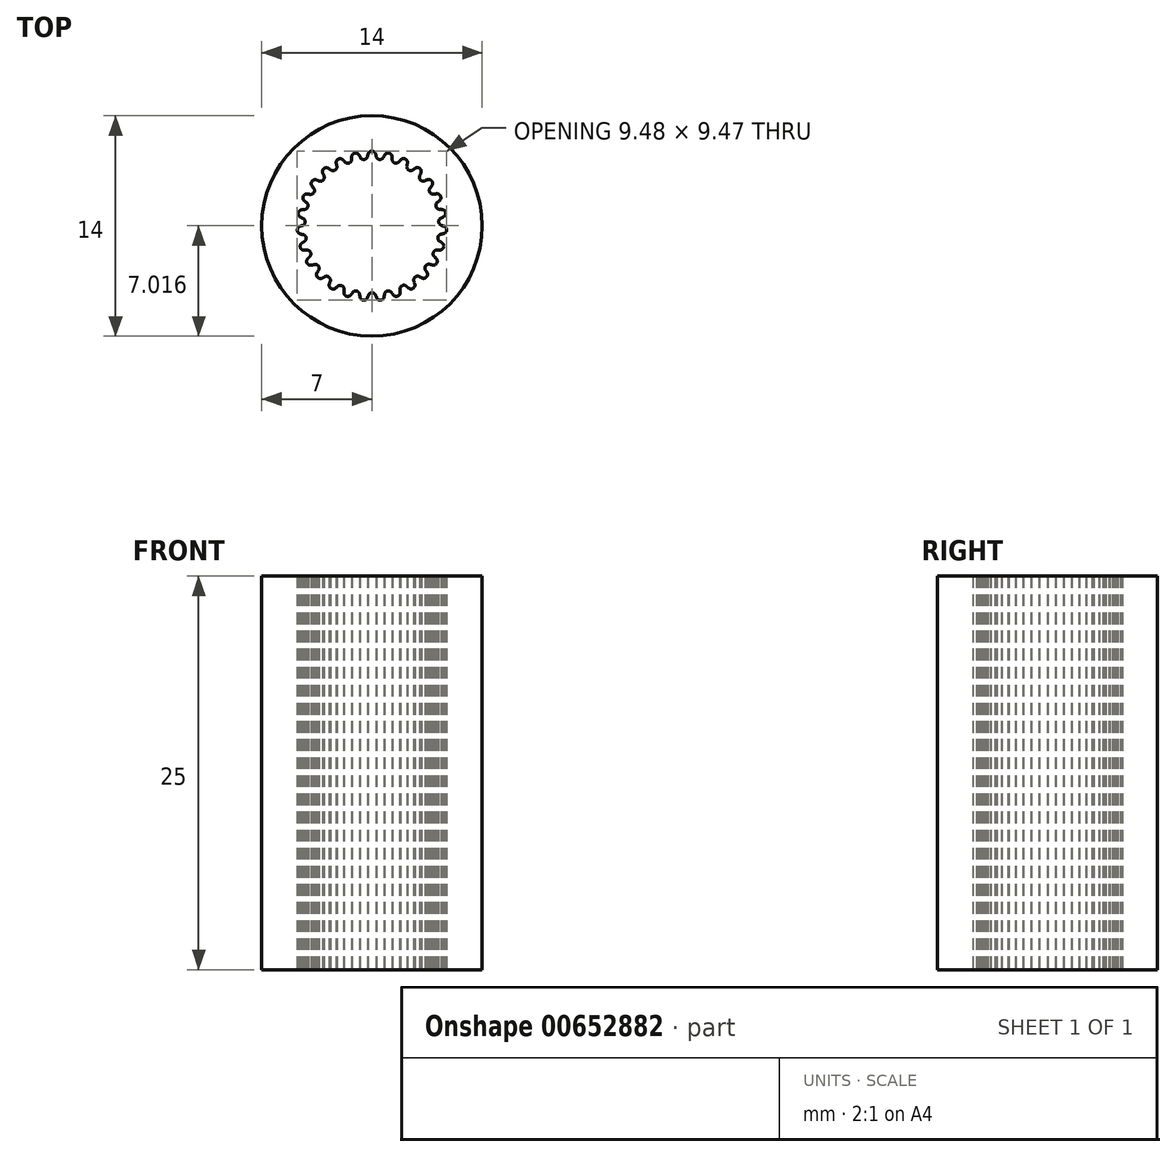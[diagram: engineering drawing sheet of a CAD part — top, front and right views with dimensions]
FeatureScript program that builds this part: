
annotation { "Feature Type Name" : "Feature", "Feature Type Description" : "" }
export const myFeature = defineFeature(function(context is Context, id is Id, definition is map)
    precondition{}
    {
        {
            var Q0;
            Q0=qCreatedBy(makeId("Top.planeOp"),FACE);
            var sketch = newSketch(context, id + "F0", { "sketchPlane" : qUnion([Q0])});
            skCircle(sketch, "E0", {"center": v(0, 0) * mm, "radius": 4.5 * mm});
            skCircle(sketch, "E1", {"center": v(0, 0) * mm, "radius": 7 * mm});
            skCircle(sketch, "E2", {"center": v(0, 4.5) * mm, "radius": 0.25 * mm});
            skCircle(sketch, "E3.1.0", {"center": v(-0.52, 4.47) * mm, "radius": 0.25 * mm});
            skCircle(sketch, "E3.2.0", {"center": v(-1.04, 4.38) * mm, "radius": 0.25 * mm});
            skCircle(sketch, "E3.3.0", {"center": v(-1.54, 4.23) * mm, "radius": 0.25 * mm});
            skCircle(sketch, "E3.4.0", {"center": v(-2.02, 4.02) * mm, "radius": 0.25 * mm});
            skCircle(sketch, "E3.5.0", {"center": v(-2.47, 3.76) * mm, "radius": 0.25 * mm});
            skCircle(sketch, "E3.6.0", {"center": v(-2.9, 3.45) * mm, "radius": 0.25 * mm});
            skCircle(sketch, "E3.7.0", {"center": v(-3.27, 3.09) * mm, "radius": 0.25 * mm});
            skCircle(sketch, "E3.8.0", {"center": v(-3.61, 2.69) * mm, "radius": 0.25 * mm});
            skCircle(sketch, "E3.9.0", {"center": v(-3.9, 2.25) * mm, "radius": 0.25 * mm});
            skCircle(sketch, "E3.10.0", {"center": v(-4.13, 1.78) * mm, "radius": 0.25 * mm});
            skCircle(sketch, "E3.11.0", {"center": v(-4.31, 1.29) * mm, "radius": 0.25 * mm});
            skCircle(sketch, "E3.12.0", {"center": v(-4.43, 0.78) * mm, "radius": 0.25 * mm});
            skCircle(sketch, "E3.13.0", {"center": v(-4.5, 0.26) * mm, "radius": 0.25 * mm});
            skCircle(sketch, "E3.14.0", {"center": v(-4.5, -0.27) * mm, "radius": 0.25 * mm});
            skCircle(sketch, "E3.15.0", {"center": v(-4.43, -0.79) * mm, "radius": 0.25 * mm});
            skCircle(sketch, "E3.16.0", {"center": v(-4.3, -1.3) * mm, "radius": 0.25 * mm});
            skCircle(sketch, "E3.17.0", {"center": v(-4.13, -1.79) * mm, "radius": 0.25 * mm});
            skCircle(sketch, "E3.18.0", {"center": v(-3.9, -2.25) * mm, "radius": 0.25 * mm});
            skCircle(sketch, "E3.19.0", {"center": v(-3.6, -2.7) * mm, "radius": 0.25 * mm});
            skLineSegment(sketch, "E3.anchor1", {"start": v(0, 0) * mm, "end": v(0, 4.5) * mm, "construction": true});
            skLineSegment(sketch, "E3.anchor2", {"start": v(0, 0) * mm, "end": v(0.5, 4.47) * mm, "construction": true});
            skCircle(sketch, "E4.1.20.0", {"center": v(-3.27, -3.1) * mm, "radius": 0.25 * mm});
            skCircle(sketch, "E4.1.21.0", {"center": v(-2.89, -3.45) * mm, "radius": 0.25 * mm});
            skCircle(sketch, "E4.1.22.0", {"center": v(-2.47, -3.76) * mm, "radius": 0.25 * mm});
            skCircle(sketch, "E4.1.23.0", {"center": v(-2.01, -4.02) * mm, "radius": 0.25 * mm});
            skCircle(sketch, "E4.1.24.0", {"center": v(-1.53, -4.23) * mm, "radius": 0.25 * mm});
            skCircle(sketch, "E4.1.25.0", {"center": v(-1.03, -4.38) * mm, "radius": 0.25 * mm});
            skCircle(sketch, "E4.1.26.0", {"center": v(-0.52, -4.47) * mm, "radius": 0.25 * mm});
            skCircle(sketch, "E4.1.27.0", {"center": v(0, -4.5) * mm, "radius": 0.25 * mm});
            skCircle(sketch, "E4.1.28.0", {"center": v(0.53, -4.47) * mm, "radius": 0.25 * mm});
            skCircle(sketch, "E4.1.29.0", {"center": v(1.04, -4.38) * mm, "radius": 0.25 * mm});
            skCircle(sketch, "E4.1.30.0", {"center": v(1.55, -4.23) * mm, "radius": 0.25 * mm});
            skCircle(sketch, "E4.1.31.0", {"center": v(2.03, -4.02) * mm, "radius": 0.25 * mm});
            skCircle(sketch, "E4.1.32.0", {"center": v(2.48, -3.76) * mm, "radius": 0.25 * mm});
            skCircle(sketch, "E4.1.33.0", {"center": v(2.9, -3.44) * mm, "radius": 0.25 * mm});
            skCircle(sketch, "E4.1.34.0", {"center": v(3.28, -3.08) * mm, "radius": 0.25 * mm});
            skCircle(sketch, "E4.1.35.0", {"center": v(3.61, -2.68) * mm, "radius": 0.25 * mm});
            skCircle(sketch, "E4.1.36.0", {"center": v(3.9, -2.24) * mm, "radius": 0.25 * mm});
            skCircle(sketch, "E4.1.37.0", {"center": v(4.14, -1.77) * mm, "radius": 0.25 * mm});
            skCircle(sketch, "E4.1.38.0", {"center": v(4.31, -1.28) * mm, "radius": 0.25 * mm});
            skCircle(sketch, "E4.1.39.0", {"center": v(4.43, -0.77) * mm, "radius": 0.25 * mm});
            skCircle(sketch, "E5.1.40.0", {"center": v(4.5, -0.25) * mm, "radius": 0.25 * mm});
            skCircle(sketch, "E5.1.41.0", {"center": v(4.5, 0.27) * mm, "radius": 0.25 * mm});
            skCircle(sketch, "E5.1.42.0", {"center": v(4.43, 0.8) * mm, "radius": 0.25 * mm});
            skCircle(sketch, "E6.1.43.0", {"center": v(4.3, 1.3) * mm, "radius": 0.25 * mm});
            skCircle(sketch, "E6.1.44.0", {"center": v(4.13, 1.8) * mm, "radius": 0.25 * mm});
            skCircle(sketch, "E7.1.45.0", {"center": v(3.9, 2.26) * mm, "radius": 0.25 * mm});
            skCircle(sketch, "E7.1.46.0", {"center": v(3.6, 2.7) * mm, "radius": 0.25 * mm});
            skCircle(sketch, "E7.1.47.0", {"center": v(3.27, 3.1) * mm, "radius": 0.25 * mm});
            skCircle(sketch, "E7.1.48.0", {"center": v(2.88, 3.45) * mm, "radius": 0.25 * mm});
            skCircle(sketch, "E7.1.49.0", {"center": v(2.46, 3.77) * mm, "radius": 0.25 * mm});
            skCircle(sketch, "E8.1.50.0", {"center": v(2, 4.03) * mm, "radius": 0.25 * mm});
            skCircle(sketch, "E8.1.51.0", {"center": v(1.53, 4.23) * mm, "radius": 0.25 * mm});
            skCircle(sketch, "E8.1.52.0", {"center": v(1.03, 4.38) * mm, "radius": 0.25 * mm});
            skCircle(sketch, "E8.1.53.0", {"center": v(0.5, 4.47) * mm, "radius": 0.25 * mm});
            skSolve(sketch);
        }
        {
            var Q0;
            Q0 = qSketchRegion(id + "F0", true);
            var Q1;
            {var subQ0=sQuery(id+"F0.wireOp",EDGE,"E4.1.33.0");var subQ1=sQuery(id+"F0.wireOp",EDGE,"E0");var subQ2=makeQuery(id+"F0.imprint","INTERSECT",VERTEX,{"disambiguationData":[OD(0.0)],"derivedFrom":[subQ1,subQ0]});Q1=makeQuery(id+"F0.imprint","IMPRINT",FACE,{"disambiguationData":[TD([[makeQuery(id+"F0.imprint","IMPRINT",EDGE,{"disambiguationData":[TD([[subQ2,-1.0]])],"derivedFrom":subQ1}),1.0]])]});}
            var Q2;
            {var subQ0=sQuery(id+"F0.wireOp",EDGE,"E4.1.33.0");var subQ1=sQuery(id+"F0.wireOp",EDGE,"E0");var subQ2=makeQuery(id+"F0.imprint","INTERSECT",VERTEX,{"disambiguationData":[OD(0.0)],"derivedFrom":[subQ1,subQ0]});Q2=makeQuery(id+"F0.imprint","IMPRINT",FACE,{"disambiguationData":[TD([[makeQuery(id+"F0.imprint","IMPRINT",EDGE,{"disambiguationData":[TD([[subQ2,-1.0]])],"derivedFrom":subQ1}),-1.0]])]});}
            var Q3;
            {var subQ0=sQuery(id+"F0.wireOp",EDGE,"E4.1.31.0");var subQ1=sQuery(id+"F0.wireOp",EDGE,"E0");var subQ2=makeQuery(id+"F0.imprint","INTERSECT",VERTEX,{"disambiguationData":[OD(0.0)],"derivedFrom":[subQ1,subQ0]});Q3=makeQuery(id+"F0.imprint","IMPRINT",FACE,{"disambiguationData":[TD([[makeQuery(id+"F0.imprint","IMPRINT",EDGE,{"disambiguationData":[TD([[subQ2,-1.0]])],"derivedFrom":subQ1}),1.0]])]});}
            var Q4;
            {var subQ0=sQuery(id+"F0.wireOp",EDGE,"E4.1.31.0");var subQ1=sQuery(id+"F0.wireOp",EDGE,"E0");var subQ2=makeQuery(id+"F0.imprint","INTERSECT",VERTEX,{"disambiguationData":[OD(0.0)],"derivedFrom":[subQ1,subQ0]});Q4=makeQuery(id+"F0.imprint","IMPRINT",FACE,{"disambiguationData":[TD([[makeQuery(id+"F0.imprint","IMPRINT",EDGE,{"disambiguationData":[TD([[subQ2,-1.0]])],"derivedFrom":subQ1}),-1.0]])]});}
            var Q5;
            {var subQ0=sQuery(id+"F0.wireOp",EDGE,"E4.1.29.0");var subQ1=sQuery(id+"F0.wireOp",EDGE,"E0");var subQ2=makeQuery(id+"F0.imprint","INTERSECT",VERTEX,{"disambiguationData":[OD(0.0)],"derivedFrom":[subQ1,subQ0]});Q5=makeQuery(id+"F0.imprint","IMPRINT",FACE,{"disambiguationData":[TD([[makeQuery(id+"F0.imprint","IMPRINT",EDGE,{"disambiguationData":[TD([[subQ2,-1.0]])],"derivedFrom":subQ1}),-1.0]])]});}
            var Q6;
            {var subQ0=sQuery(id+"F0.wireOp",EDGE,"E4.1.29.0");var subQ1=sQuery(id+"F0.wireOp",EDGE,"E0");var subQ2=makeQuery(id+"F0.imprint","INTERSECT",VERTEX,{"disambiguationData":[OD(0.0)],"derivedFrom":[subQ1,subQ0]});Q6=makeQuery(id+"F0.imprint","IMPRINT",FACE,{"disambiguationData":[TD([[makeQuery(id+"F0.imprint","IMPRINT",EDGE,{"disambiguationData":[TD([[subQ2,-1.0]])],"derivedFrom":subQ1}),1.0]])]});}
            var Q7;
            {var subQ0=sQuery(id+"F0.wireOp",EDGE,"E4.1.27.0");var subQ1=sQuery(id+"F0.wireOp",EDGE,"E0");var subQ2=makeQuery(id+"F0.imprint","INTERSECT",VERTEX,{"disambiguationData":[OD(0.0)],"derivedFrom":[subQ1,subQ0]});Q7=makeQuery(id+"F0.imprint","IMPRINT",FACE,{"disambiguationData":[TD([[makeQuery(id+"F0.imprint","IMPRINT",EDGE,{"disambiguationData":[TD([[subQ2,-1.0]])],"derivedFrom":subQ1}),1.0]])]});}
            var Q8;
            {var subQ0=sQuery(id+"F0.wireOp",EDGE,"E4.1.27.0");var subQ1=sQuery(id+"F0.wireOp",EDGE,"E0");var subQ2=makeQuery(id+"F0.imprint","INTERSECT",VERTEX,{"disambiguationData":[OD(0.0)],"derivedFrom":[subQ1,subQ0]});Q8=makeQuery(id+"F0.imprint","IMPRINT",FACE,{"disambiguationData":[TD([[makeQuery(id+"F0.imprint","IMPRINT",EDGE,{"disambiguationData":[TD([[subQ2,-1.0]])],"derivedFrom":subQ1}),-1.0]])]});}
            var Q9;
            {var subQ0=sQuery(id+"F0.wireOp",EDGE,"E4.1.25.0");var subQ1=sQuery(id+"F0.wireOp",EDGE,"E0");var subQ2=makeQuery(id+"F0.imprint","INTERSECT",VERTEX,{"disambiguationData":[OD(0.0)],"derivedFrom":[subQ1,subQ0]});Q9=makeQuery(id+"F0.imprint","IMPRINT",FACE,{"disambiguationData":[TD([[makeQuery(id+"F0.imprint","IMPRINT",EDGE,{"disambiguationData":[TD([[subQ2,-1.0]])],"derivedFrom":subQ1}),1.0]])]});}
            var Q10;
            {var subQ0=sQuery(id+"F0.wireOp",EDGE,"E4.1.25.0");var subQ1=sQuery(id+"F0.wireOp",EDGE,"E0");var subQ2=makeQuery(id+"F0.imprint","INTERSECT",VERTEX,{"disambiguationData":[OD(0.0)],"derivedFrom":[subQ1,subQ0]});Q10=makeQuery(id+"F0.imprint","IMPRINT",FACE,{"disambiguationData":[TD([[makeQuery(id+"F0.imprint","IMPRINT",EDGE,{"disambiguationData":[TD([[subQ2,-1.0]])],"derivedFrom":subQ1}),-1.0]])]});}
            var Q11;
            {var subQ0=sQuery(id+"F0.wireOp",EDGE,"E4.1.35.0");var subQ1=sQuery(id+"F0.wireOp",EDGE,"E0");var subQ2=makeQuery(id+"F0.imprint","INTERSECT",VERTEX,{"disambiguationData":[OD(0.0)],"derivedFrom":[subQ1,subQ0]});Q11=makeQuery(id+"F0.imprint","IMPRINT",FACE,{"disambiguationData":[TD([[makeQuery(id+"F0.imprint","IMPRINT",EDGE,{"disambiguationData":[TD([[subQ2,-1.0]])],"derivedFrom":subQ1}),1.0]])]});}
            var Q12;
            {var subQ0=sQuery(id+"F0.wireOp",EDGE,"E4.1.35.0");var subQ1=sQuery(id+"F0.wireOp",EDGE,"E0");var subQ2=makeQuery(id+"F0.imprint","INTERSECT",VERTEX,{"disambiguationData":[OD(0.0)],"derivedFrom":[subQ1,subQ0]});Q12=makeQuery(id+"F0.imprint","IMPRINT",FACE,{"disambiguationData":[TD([[makeQuery(id+"F0.imprint","IMPRINT",EDGE,{"disambiguationData":[TD([[subQ2,-1.0]])],"derivedFrom":subQ1}),-1.0]])]});}
            var Q13;
            {var subQ0=sQuery(id+"F0.wireOp",EDGE,"E4.1.37.0");var subQ1=sQuery(id+"F0.wireOp",EDGE,"E0");var subQ2=makeQuery(id+"F0.imprint","INTERSECT",VERTEX,{"disambiguationData":[OD(0.0)],"derivedFrom":[subQ1,subQ0]});Q13=makeQuery(id+"F0.imprint","IMPRINT",FACE,{"disambiguationData":[TD([[makeQuery(id+"F0.imprint","IMPRINT",EDGE,{"disambiguationData":[TD([[subQ2,-1.0]])],"derivedFrom":subQ1}),1.0]])]});}
            var Q14;
            {var subQ0=sQuery(id+"F0.wireOp",EDGE,"E4.1.37.0");var subQ1=sQuery(id+"F0.wireOp",EDGE,"E0");var subQ2=makeQuery(id+"F0.imprint","INTERSECT",VERTEX,{"disambiguationData":[OD(0.0)],"derivedFrom":[subQ1,subQ0]});Q14=makeQuery(id+"F0.imprint","IMPRINT",FACE,{"disambiguationData":[TD([[makeQuery(id+"F0.imprint","IMPRINT",EDGE,{"disambiguationData":[TD([[subQ2,-1.0]])],"derivedFrom":subQ1}),-1.0]])]});}
            var Q15;
            {var subQ0=sQuery(id+"F0.wireOp",EDGE,"E4.1.39.0");var subQ1=sQuery(id+"F0.wireOp",EDGE,"E0");var subQ2=makeQuery(id+"F0.imprint","INTERSECT",VERTEX,{"disambiguationData":[OD(0.0)],"derivedFrom":[subQ1,subQ0]});Q15=makeQuery(id+"F0.imprint","IMPRINT",FACE,{"disambiguationData":[TD([[makeQuery(id+"F0.imprint","IMPRINT",EDGE,{"disambiguationData":[TD([[subQ2,-1.0]])],"derivedFrom":subQ1}),-1.0]])]});}
            var Q16;
            {var subQ0=sQuery(id+"F0.wireOp",EDGE,"E5.1.41.0");var subQ1=sQuery(id+"F0.wireOp",EDGE,"E0");var subQ2=makeQuery(id+"F0.imprint","INTERSECT",VERTEX,{"disambiguationData":[OD(0.0)],"derivedFrom":[subQ1,subQ0]});Q16=makeQuery(id+"F0.imprint","IMPRINT",FACE,{"disambiguationData":[TD([[makeQuery(id+"F0.imprint","IMPRINT",EDGE,{"disambiguationData":[TD([[subQ2,-1.0]])],"derivedFrom":subQ1}),-1.0]])]});}
            var Q17;
            {var subQ0=sQuery(id+"F0.wireOp",EDGE,"E4.1.39.0");var subQ1=sQuery(id+"F0.wireOp",EDGE,"E0");var subQ2=makeQuery(id+"F0.imprint","INTERSECT",VERTEX,{"disambiguationData":[OD(0.0)],"derivedFrom":[subQ1,subQ0]});Q17=makeQuery(id+"F0.imprint","IMPRINT",FACE,{"disambiguationData":[TD([[makeQuery(id+"F0.imprint","IMPRINT",EDGE,{"disambiguationData":[TD([[subQ2,-1.0]])],"derivedFrom":subQ1}),1.0]])]});}
            var Q18;
            {var subQ0=sQuery(id+"F0.wireOp",EDGE,"E6.1.43.0");var subQ1=sQuery(id+"F0.wireOp",EDGE,"E0");var subQ2=makeQuery(id+"F0.imprint","INTERSECT",VERTEX,{"disambiguationData":[OD(0.0)],"derivedFrom":[subQ1,subQ0]});Q18=makeQuery(id+"F0.imprint","IMPRINT",FACE,{"disambiguationData":[TD([[makeQuery(id+"F0.imprint","IMPRINT",EDGE,{"disambiguationData":[TD([[subQ2,-1.0]])],"derivedFrom":subQ1}),-1.0]])]});}
            var Q19;
            {var subQ0=sQuery(id+"F0.wireOp",EDGE,"E6.1.43.0");var subQ1=sQuery(id+"F0.wireOp",EDGE,"E0");var subQ2=makeQuery(id+"F0.imprint","INTERSECT",VERTEX,{"disambiguationData":[OD(0.0)],"derivedFrom":[subQ1,subQ0]});Q19=makeQuery(id+"F0.imprint","IMPRINT",FACE,{"disambiguationData":[TD([[makeQuery(id+"F0.imprint","IMPRINT",EDGE,{"disambiguationData":[TD([[subQ2,-1.0]])],"derivedFrom":subQ1}),1.0]])]});}
            var Q20;
            {var subQ0=sQuery(id+"F0.wireOp",EDGE,"E7.1.47.0");var subQ1=sQuery(id+"F0.wireOp",EDGE,"E0");var subQ2=makeQuery(id+"F0.imprint","INTERSECT",VERTEX,{"disambiguationData":[OD(0.0)],"derivedFrom":[subQ1,subQ0]});Q20=makeQuery(id+"F0.imprint","IMPRINT",FACE,{"disambiguationData":[TD([[makeQuery(id+"F0.imprint","IMPRINT",EDGE,{"disambiguationData":[TD([[subQ2,-1.0]])],"derivedFrom":subQ1}),-1.0]])]});}
            var Q21;
            {var subQ0=sQuery(id+"F0.wireOp",EDGE,"E7.1.49.0");var subQ1=sQuery(id+"F0.wireOp",EDGE,"E0");var subQ2=makeQuery(id+"F0.imprint","INTERSECT",VERTEX,{"disambiguationData":[OD(0.0)],"derivedFrom":[subQ1,subQ0]});Q21=makeQuery(id+"F0.imprint","IMPRINT",FACE,{"disambiguationData":[TD([[makeQuery(id+"F0.imprint","IMPRINT",EDGE,{"disambiguationData":[TD([[subQ2,-1.0]])],"derivedFrom":subQ1}),-1.0]])]});}
            var Q22;
            {var subQ0=sQuery(id+"F0.wireOp",EDGE,"E7.1.49.0");var subQ1=sQuery(id+"F0.wireOp",EDGE,"E0");var subQ2=makeQuery(id+"F0.imprint","INTERSECT",VERTEX,{"disambiguationData":[OD(0.0)],"derivedFrom":[subQ1,subQ0]});Q22=makeQuery(id+"F0.imprint","IMPRINT",FACE,{"disambiguationData":[TD([[makeQuery(id+"F0.imprint","IMPRINT",EDGE,{"disambiguationData":[TD([[subQ2,-1.0]])],"derivedFrom":subQ1}),1.0]])]});}
            var Q23;
            {var subQ0=sQuery(id+"F0.wireOp",EDGE,"E3.1.0");var subQ1=sQuery(id+"F0.wireOp",EDGE,"E0");var subQ2=makeQuery(id+"F0.imprint","INTERSECT",VERTEX,{"disambiguationData":[OD(0.0)],"derivedFrom":[subQ1,subQ0]});Q23=makeQuery(id+"F0.imprint","IMPRINT",FACE,{"disambiguationData":[TD([[makeQuery(id+"F0.imprint","IMPRINT",EDGE,{"disambiguationData":[TD([[subQ2,-1.0]])],"derivedFrom":subQ1}),1.0]])]});}
            var Q24;
            {var subQ0=sQuery(id+"F0.wireOp",EDGE,"E3.1.0");var subQ1=sQuery(id+"F0.wireOp",EDGE,"E0");var subQ2=makeQuery(id+"F0.imprint","INTERSECT",VERTEX,{"disambiguationData":[OD(0.0)],"derivedFrom":[subQ1,subQ0]});Q24=makeQuery(id+"F0.imprint","IMPRINT",FACE,{"disambiguationData":[TD([[makeQuery(id+"F0.imprint","IMPRINT",EDGE,{"disambiguationData":[TD([[subQ2,-1.0]])],"derivedFrom":subQ1}),-1.0]])]});}
            var Q25;
            {var subQ0=sQuery(id+"F0.wireOp",EDGE,"E3.3.0");var subQ1=sQuery(id+"F0.wireOp",EDGE,"E0");var subQ2=makeQuery(id+"F0.imprint","INTERSECT",VERTEX,{"disambiguationData":[OD(0.0)],"derivedFrom":[subQ1,subQ0]});Q25=makeQuery(id+"F0.imprint","IMPRINT",FACE,{"disambiguationData":[TD([[makeQuery(id+"F0.imprint","IMPRINT",EDGE,{"disambiguationData":[TD([[subQ2,-1.0]])],"derivedFrom":subQ1}),-1.0]])]});}
            var Q26;
            {var subQ0=sQuery(id+"F0.wireOp",EDGE,"E3.3.0");var subQ1=sQuery(id+"F0.wireOp",EDGE,"E0");var subQ2=makeQuery(id+"F0.imprint","INTERSECT",VERTEX,{"disambiguationData":[OD(0.0)],"derivedFrom":[subQ1,subQ0]});Q26=makeQuery(id+"F0.imprint","IMPRINT",FACE,{"disambiguationData":[TD([[makeQuery(id+"F0.imprint","IMPRINT",EDGE,{"disambiguationData":[TD([[subQ2,-1.0]])],"derivedFrom":subQ1}),1.0]])]});}
            var Q27;
            {var subQ0=sQuery(id+"F0.wireOp",EDGE,"E4.1.23.0");var subQ1=sQuery(id+"F0.wireOp",EDGE,"E0");var subQ2=makeQuery(id+"F0.imprint","INTERSECT",VERTEX,{"disambiguationData":[OD(0.0)],"derivedFrom":[subQ1,subQ0]});Q27=makeQuery(id+"F0.imprint","IMPRINT",FACE,{"disambiguationData":[TD([[makeQuery(id+"F0.imprint","IMPRINT",EDGE,{"disambiguationData":[TD([[subQ2,-1.0]])],"derivedFrom":subQ1}),-1.0]])]});}
            var Q28;
            {var subQ0=sQuery(id+"F0.wireOp",EDGE,"E4.1.23.0");var subQ1=sQuery(id+"F0.wireOp",EDGE,"E0");var subQ2=makeQuery(id+"F0.imprint","INTERSECT",VERTEX,{"disambiguationData":[OD(0.0)],"derivedFrom":[subQ1,subQ0]});Q28=makeQuery(id+"F0.imprint","IMPRINT",FACE,{"disambiguationData":[TD([[makeQuery(id+"F0.imprint","IMPRINT",EDGE,{"disambiguationData":[TD([[subQ2,-1.0]])],"derivedFrom":subQ1}),1.0]])]});}
            var Q29;
            {var subQ0=sQuery(id+"F0.wireOp",EDGE,"E4.1.21.0");var subQ1=sQuery(id+"F0.wireOp",EDGE,"E0");var subQ2=makeQuery(id+"F0.imprint","INTERSECT",VERTEX,{"disambiguationData":[OD(0.0)],"derivedFrom":[subQ1,subQ0]});Q29=makeQuery(id+"F0.imprint","IMPRINT",FACE,{"disambiguationData":[TD([[makeQuery(id+"F0.imprint","IMPRINT",EDGE,{"disambiguationData":[TD([[subQ2,-1.0]])],"derivedFrom":subQ1}),-1.0]])]});}
            var Q30;
            {var subQ0=sQuery(id+"F0.wireOp",EDGE,"E4.1.21.0");var subQ1=sQuery(id+"F0.wireOp",EDGE,"E0");var subQ2=makeQuery(id+"F0.imprint","INTERSECT",VERTEX,{"disambiguationData":[OD(0.0)],"derivedFrom":[subQ1,subQ0]});Q30=makeQuery(id+"F0.imprint","IMPRINT",FACE,{"disambiguationData":[TD([[makeQuery(id+"F0.imprint","IMPRINT",EDGE,{"disambiguationData":[TD([[subQ2,-1.0]])],"derivedFrom":subQ1}),1.0]])]});}
            var Q31;
            {var subQ0=sQuery(id+"F0.wireOp",EDGE,"E3.17.0");var subQ1=sQuery(id+"F0.wireOp",EDGE,"E0");var subQ2=makeQuery(id+"F0.imprint","INTERSECT",VERTEX,{"disambiguationData":[OD(0.0)],"derivedFrom":[subQ1,subQ0]});Q31=makeQuery(id+"F0.imprint","IMPRINT",FACE,{"disambiguationData":[TD([[makeQuery(id+"F0.imprint","IMPRINT",EDGE,{"disambiguationData":[TD([[subQ2,-1.0]])],"derivedFrom":subQ1}),-1.0]])]});}
            var Q32;
            {var subQ0=sQuery(id+"F0.wireOp",EDGE,"E3.17.0");var subQ1=sQuery(id+"F0.wireOp",EDGE,"E0");var subQ2=makeQuery(id+"F0.imprint","INTERSECT",VERTEX,{"disambiguationData":[OD(0.0)],"derivedFrom":[subQ1,subQ0]});Q32=makeQuery(id+"F0.imprint","IMPRINT",FACE,{"disambiguationData":[TD([[makeQuery(id+"F0.imprint","IMPRINT",EDGE,{"disambiguationData":[TD([[subQ2,-1.0]])],"derivedFrom":subQ1}),1.0]])]});}
            var Q33;
            {var subQ0=sQuery(id+"F0.wireOp",EDGE,"E3.15.0");var subQ1=sQuery(id+"F0.wireOp",EDGE,"E0");var subQ2=makeQuery(id+"F0.imprint","INTERSECT",VERTEX,{"disambiguationData":[OD(0.0)],"derivedFrom":[subQ1,subQ0]});Q33=makeQuery(id+"F0.imprint","IMPRINT",FACE,{"disambiguationData":[TD([[makeQuery(id+"F0.imprint","IMPRINT",EDGE,{"disambiguationData":[TD([[subQ2,-1.0]])],"derivedFrom":subQ1}),-1.0]])]});}
            var Q34;
            {var subQ0=sQuery(id+"F0.wireOp",EDGE,"E3.15.0");var subQ1=sQuery(id+"F0.wireOp",EDGE,"E0");var subQ2=makeQuery(id+"F0.imprint","INTERSECT",VERTEX,{"disambiguationData":[OD(0.0)],"derivedFrom":[subQ1,subQ0]});Q34=makeQuery(id+"F0.imprint","IMPRINT",FACE,{"disambiguationData":[TD([[makeQuery(id+"F0.imprint","IMPRINT",EDGE,{"disambiguationData":[TD([[subQ2,-1.0]])],"derivedFrom":subQ1}),1.0]])]});}
            var Q35;
            {var subQ0=sQuery(id+"F0.wireOp",EDGE,"E3.13.0");var subQ1=sQuery(id+"F0.wireOp",EDGE,"E0");var subQ2=makeQuery(id+"F0.imprint","INTERSECT",VERTEX,{"disambiguationData":[OD(0.0)],"derivedFrom":[subQ1,subQ0]});Q35=makeQuery(id+"F0.imprint","IMPRINT",FACE,{"disambiguationData":[TD([[makeQuery(id+"F0.imprint","IMPRINT",EDGE,{"disambiguationData":[TD([[subQ2,-1.0]])],"derivedFrom":subQ1}),-1.0]])]});}
            var Q36;
            {var subQ0=sQuery(id+"F0.wireOp",EDGE,"E3.13.0");var subQ1=sQuery(id+"F0.wireOp",EDGE,"E0");var subQ2=makeQuery(id+"F0.imprint","INTERSECT",VERTEX,{"disambiguationData":[OD(0.0)],"derivedFrom":[subQ1,subQ0]});Q36=makeQuery(id+"F0.imprint","IMPRINT",FACE,{"disambiguationData":[TD([[makeQuery(id+"F0.imprint","IMPRINT",EDGE,{"disambiguationData":[TD([[subQ2,-1.0]])],"derivedFrom":subQ1}),1.0]])]});}
            var Q37;
            {var subQ0=sQuery(id+"F0.wireOp",EDGE,"E3.19.0");var subQ1=sQuery(id+"F0.wireOp",EDGE,"E0");var subQ2=makeQuery(id+"F0.imprint","INTERSECT",VERTEX,{"disambiguationData":[OD(0.0)],"derivedFrom":[subQ1,subQ0]});Q37=makeQuery(id+"F0.imprint","IMPRINT",FACE,{"disambiguationData":[TD([[makeQuery(id+"F0.imprint","IMPRINT",EDGE,{"disambiguationData":[TD([[subQ2,-1.0]])],"derivedFrom":subQ1}),-1.0]])]});}
            var Q38;
            {var subQ0=sQuery(id+"F0.wireOp",EDGE,"E3.19.0");var subQ1=sQuery(id+"F0.wireOp",EDGE,"E0");var subQ2=makeQuery(id+"F0.imprint","INTERSECT",VERTEX,{"disambiguationData":[OD(0.0)],"derivedFrom":[subQ1,subQ0]});Q38=makeQuery(id+"F0.imprint","IMPRINT",FACE,{"disambiguationData":[TD([[makeQuery(id+"F0.imprint","IMPRINT",EDGE,{"disambiguationData":[TD([[subQ2,-1.0]])],"derivedFrom":subQ1}),1.0]])]});}
            var Q39;
            {var subQ0=sQuery(id+"F0.wireOp",EDGE,"E3.11.0");var subQ1=sQuery(id+"F0.wireOp",EDGE,"E0");var subQ2=makeQuery(id+"F0.imprint","INTERSECT",VERTEX,{"disambiguationData":[OD(0.0)],"derivedFrom":[subQ1,subQ0]});Q39=makeQuery(id+"F0.imprint","IMPRINT",FACE,{"disambiguationData":[TD([[makeQuery(id+"F0.imprint","IMPRINT",EDGE,{"disambiguationData":[TD([[subQ2,-1.0]])],"derivedFrom":subQ1}),-1.0]])]});}
            var Q40;
            {var subQ0=sQuery(id+"F0.wireOp",EDGE,"E3.11.0");var subQ1=sQuery(id+"F0.wireOp",EDGE,"E0");var subQ2=makeQuery(id+"F0.imprint","INTERSECT",VERTEX,{"disambiguationData":[OD(0.0)],"derivedFrom":[subQ1,subQ0]});Q40=makeQuery(id+"F0.imprint","IMPRINT",FACE,{"disambiguationData":[TD([[makeQuery(id+"F0.imprint","IMPRINT",EDGE,{"disambiguationData":[TD([[subQ2,-1.0]])],"derivedFrom":subQ1}),1.0]])]});}
            var Q41;
            {var subQ0=sQuery(id+"F0.wireOp",EDGE,"E3.9.0");var subQ1=sQuery(id+"F0.wireOp",EDGE,"E0");var subQ2=makeQuery(id+"F0.imprint","INTERSECT",VERTEX,{"disambiguationData":[OD(0.0)],"derivedFrom":[subQ1,subQ0]});Q41=makeQuery(id+"F0.imprint","IMPRINT",FACE,{"disambiguationData":[TD([[makeQuery(id+"F0.imprint","IMPRINT",EDGE,{"disambiguationData":[TD([[subQ2,-1.0]])],"derivedFrom":subQ1}),-1.0]])]});}
            var Q42;
            {var subQ0=sQuery(id+"F0.wireOp",EDGE,"E3.9.0");var subQ1=sQuery(id+"F0.wireOp",EDGE,"E0");var subQ2=makeQuery(id+"F0.imprint","INTERSECT",VERTEX,{"disambiguationData":[OD(0.0)],"derivedFrom":[subQ1,subQ0]});Q42=makeQuery(id+"F0.imprint","IMPRINT",FACE,{"disambiguationData":[TD([[makeQuery(id+"F0.imprint","IMPRINT",EDGE,{"disambiguationData":[TD([[subQ2,-1.0]])],"derivedFrom":subQ1}),1.0]])]});}
            var Q43;
            {var subQ0=sQuery(id+"F0.wireOp",EDGE,"E3.7.0");var subQ1=sQuery(id+"F0.wireOp",EDGE,"E0");var subQ2=makeQuery(id+"F0.imprint","INTERSECT",VERTEX,{"disambiguationData":[OD(0.0)],"derivedFrom":[subQ1,subQ0]});Q43=makeQuery(id+"F0.imprint","IMPRINT",FACE,{"disambiguationData":[TD([[makeQuery(id+"F0.imprint","IMPRINT",EDGE,{"disambiguationData":[TD([[subQ2,-1.0]])],"derivedFrom":subQ1}),-1.0]])]});}
            var Q44;
            {var subQ0=sQuery(id+"F0.wireOp",EDGE,"E3.7.0");var subQ1=sQuery(id+"F0.wireOp",EDGE,"E0");var subQ2=makeQuery(id+"F0.imprint","INTERSECT",VERTEX,{"disambiguationData":[OD(0.0)],"derivedFrom":[subQ1,subQ0]});Q44=makeQuery(id+"F0.imprint","IMPRINT",FACE,{"disambiguationData":[TD([[makeQuery(id+"F0.imprint","IMPRINT",EDGE,{"disambiguationData":[TD([[subQ2,-1.0]])],"derivedFrom":subQ1}),1.0]])]});}
            var Q45;
            {var subQ0=sQuery(id+"F0.wireOp",EDGE,"E3.5.0");var subQ1=sQuery(id+"F0.wireOp",EDGE,"E0");var subQ2=makeQuery(id+"F0.imprint","INTERSECT",VERTEX,{"disambiguationData":[OD(0.0)],"derivedFrom":[subQ1,subQ0]});Q45=makeQuery(id+"F0.imprint","IMPRINT",FACE,{"disambiguationData":[TD([[makeQuery(id+"F0.imprint","IMPRINT",EDGE,{"disambiguationData":[TD([[subQ2,-1.0]])],"derivedFrom":subQ1}),-1.0]])]});}
            var Q46;
            {var subQ0=sQuery(id+"F0.wireOp",EDGE,"E3.5.0");var subQ1=sQuery(id+"F0.wireOp",EDGE,"E0");var subQ2=makeQuery(id+"F0.imprint","INTERSECT",VERTEX,{"disambiguationData":[OD(0.0)],"derivedFrom":[subQ1,subQ0]});Q46=makeQuery(id+"F0.imprint","IMPRINT",FACE,{"disambiguationData":[TD([[makeQuery(id+"F0.imprint","IMPRINT",EDGE,{"disambiguationData":[TD([[subQ2,-1.0]])],"derivedFrom":subQ1}),1.0]])]});}
            var Q47;
            {var subQ0=sQuery(id+"F0.wireOp",EDGE,"E7.1.47.0");var subQ1=sQuery(id+"F0.wireOp",EDGE,"E0");var subQ2=makeQuery(id+"F0.imprint","INTERSECT",VERTEX,{"disambiguationData":[OD(0.0)],"derivedFrom":[subQ1,subQ0]});Q47=makeQuery(id+"F0.imprint","IMPRINT",FACE,{"disambiguationData":[TD([[makeQuery(id+"F0.imprint","IMPRINT",EDGE,{"disambiguationData":[TD([[subQ2,-1.0]])],"derivedFrom":subQ1}),1.0]])]});}
            var Q48;
            {var subQ0=sQuery(id+"F0.wireOp",EDGE,"E7.1.45.0");var subQ1=sQuery(id+"F0.wireOp",EDGE,"E0");var subQ2=makeQuery(id+"F0.imprint","INTERSECT",VERTEX,{"disambiguationData":[OD(0.0)],"derivedFrom":[subQ1,subQ0]});Q48=makeQuery(id+"F0.imprint","IMPRINT",FACE,{"disambiguationData":[TD([[makeQuery(id+"F0.imprint","IMPRINT",EDGE,{"disambiguationData":[TD([[subQ2,-1.0]])],"derivedFrom":subQ1}),-1.0]])]});}
            var Q49;
            {var subQ0=sQuery(id+"F0.wireOp",EDGE,"E7.1.45.0");var subQ1=sQuery(id+"F0.wireOp",EDGE,"E0");var subQ2=makeQuery(id+"F0.imprint","INTERSECT",VERTEX,{"disambiguationData":[OD(0.0)],"derivedFrom":[subQ1,subQ0]});Q49=makeQuery(id+"F0.imprint","IMPRINT",FACE,{"disambiguationData":[TD([[makeQuery(id+"F0.imprint","IMPRINT",EDGE,{"disambiguationData":[TD([[subQ2,-1.0]])],"derivedFrom":subQ1}),1.0]])]});}
            var Q50;
            {var subQ0=sQuery(id+"F0.wireOp",EDGE,"E8.1.53.0");var subQ1=sQuery(id+"F0.wireOp",EDGE,"E0");var subQ2=makeQuery(id+"F0.imprint","INTERSECT",VERTEX,{"disambiguationData":[OD(0.0)],"derivedFrom":[subQ1,subQ0]});Q50=makeQuery(id+"F0.imprint","IMPRINT",FACE,{"disambiguationData":[TD([[makeQuery(id+"F0.imprint","IMPRINT",EDGE,{"disambiguationData":[TD([[subQ2,-1.0]])],"derivedFrom":subQ1}),1.0]])]});}
            var Q51;
            {var subQ0=sQuery(id+"F0.wireOp",EDGE,"E8.1.53.0");var subQ1=sQuery(id+"F0.wireOp",EDGE,"E0");var subQ2=makeQuery(id+"F0.imprint","INTERSECT",VERTEX,{"disambiguationData":[OD(0.0)],"derivedFrom":[subQ1,subQ0]});Q51=makeQuery(id+"F0.imprint","IMPRINT",FACE,{"disambiguationData":[TD([[makeQuery(id+"F0.imprint","IMPRINT",EDGE,{"disambiguationData":[TD([[subQ2,-1.0]])],"derivedFrom":subQ1}),-1.0]])]});}
            var Q52;
            {var subQ0=sQuery(id+"F0.wireOp",EDGE,"E8.1.51.0");var subQ1=sQuery(id+"F0.wireOp",EDGE,"E0");var subQ2=makeQuery(id+"F0.imprint","INTERSECT",VERTEX,{"disambiguationData":[OD(0.0)],"derivedFrom":[subQ1,subQ0]});Q52=makeQuery(id+"F0.imprint","IMPRINT",FACE,{"disambiguationData":[TD([[makeQuery(id+"F0.imprint","IMPRINT",EDGE,{"disambiguationData":[TD([[subQ2,-1.0]])],"derivedFrom":subQ1}),1.0]])]});}
            var Q53;
            {var subQ0=sQuery(id+"F0.wireOp",EDGE,"E8.1.51.0");var subQ1=sQuery(id+"F0.wireOp",EDGE,"E0");var subQ2=makeQuery(id+"F0.imprint","INTERSECT",VERTEX,{"disambiguationData":[OD(0.0)],"derivedFrom":[subQ1,subQ0]});Q53=makeQuery(id+"F0.imprint","IMPRINT",FACE,{"disambiguationData":[TD([[makeQuery(id+"F0.imprint","IMPRINT",EDGE,{"disambiguationData":[TD([[subQ2,-1.0]])],"derivedFrom":subQ1}),-1.0]])]});}
            var Q54;
            {var subQ0=sQuery(id+"F0.wireOp",EDGE,"E5.1.41.0");var subQ1=sQuery(id+"F0.wireOp",EDGE,"E0");var subQ2=makeQuery(id+"F0.imprint","INTERSECT",VERTEX,{"disambiguationData":[OD(0.0)],"derivedFrom":[subQ1,subQ0]});Q54=makeQuery(id+"F0.imprint","IMPRINT",FACE,{"disambiguationData":[TD([[makeQuery(id+"F0.imprint","IMPRINT",EDGE,{"disambiguationData":[TD([[subQ2,1.0]])],"derivedFrom":subQ1}),1.0]])]});}
            var Q55;
            {var subQ0=sQuery(id+"F0.wireOp",EDGE,"E5.1.41.0");var subQ1=sQuery(id+"F0.wireOp",EDGE,"E0");var subQ2=makeQuery(id+"F0.imprint","INTERSECT",VERTEX,{"disambiguationData":[OD(0.0)],"derivedFrom":[subQ1,subQ0]});Q55=makeQuery(id+"F0.imprint","IMPRINT",FACE,{"disambiguationData":[TD([[makeQuery(id+"F0.imprint","IMPRINT",EDGE,{"disambiguationData":[TD([[subQ2,1.0]])],"derivedFrom":subQ1}),-1.0]])]});}
            extrude(context, id + "F1", {"entities" : qUnion([Q0, Q1, Q2, Q3, Q4, Q5, Q6, Q7, Q8, Q9, Q10, Q11, Q12, Q13, Q14, Q15, Q16, Q17, Q18, Q19, Q20, Q21, Q22, Q23, Q24, Q25, Q26, Q27, Q28, Q29, Q30, Q31, Q32, Q33, Q34, Q35, Q36, Q37, Q38, Q39, Q40, Q41, Q42, Q43, Q44, Q45, Q46, Q47, Q48, Q49, Q50, Q51, Q52, Q53, Q54, Q55]), "depth" : 25 * mm, "offsetDistance" : 25 * mm});
        }
    });
